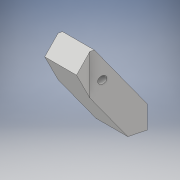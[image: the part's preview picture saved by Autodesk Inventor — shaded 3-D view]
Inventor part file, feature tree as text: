
AUTODESK INVENTOR PART (.ipt)
format: ipt  version: 2017 (Build 210142000, 142)  size: 120,320 bytes
history: native  units: mm
features: plane x5, extrude x2, split x2, sketch x2
ambient origin geometry x8: Origin, YZ Plane, XZ Plane, XY Plane, X Axis, Y Axis, Z Axis, Center Point
bodies: Solid1 (feature_tree)
feature tree (11):
  extrude  "Extrusion1"  Depth=24.14663mm
  plane  "Work Plane1"
  extrude  "Extrusion3"  Depth=22.126mm
  plane  "Work Plane9"
  plane  "Work Plane10"
  plane  "Work Plane11"
  split  "Split7"
  split  "Split8"
  sketch  "Sketch1"  dims[d0=24.14663mm d1=24.14663mm]
  sketch  "Sketch3"  dims[d2=15.316mm d3=22.126mm d4=15.0mm d5=2.563889mm d6=40.0mm d7=0.0mm d11=3.5mm d12=26.666667mm d13=13.333333mm d14=15.0mm d15=2.0mm d16=0.0mm d22=5.934119mm d23=6.0mm d24=-6.0mm]
  plane  "Work Plane8"
